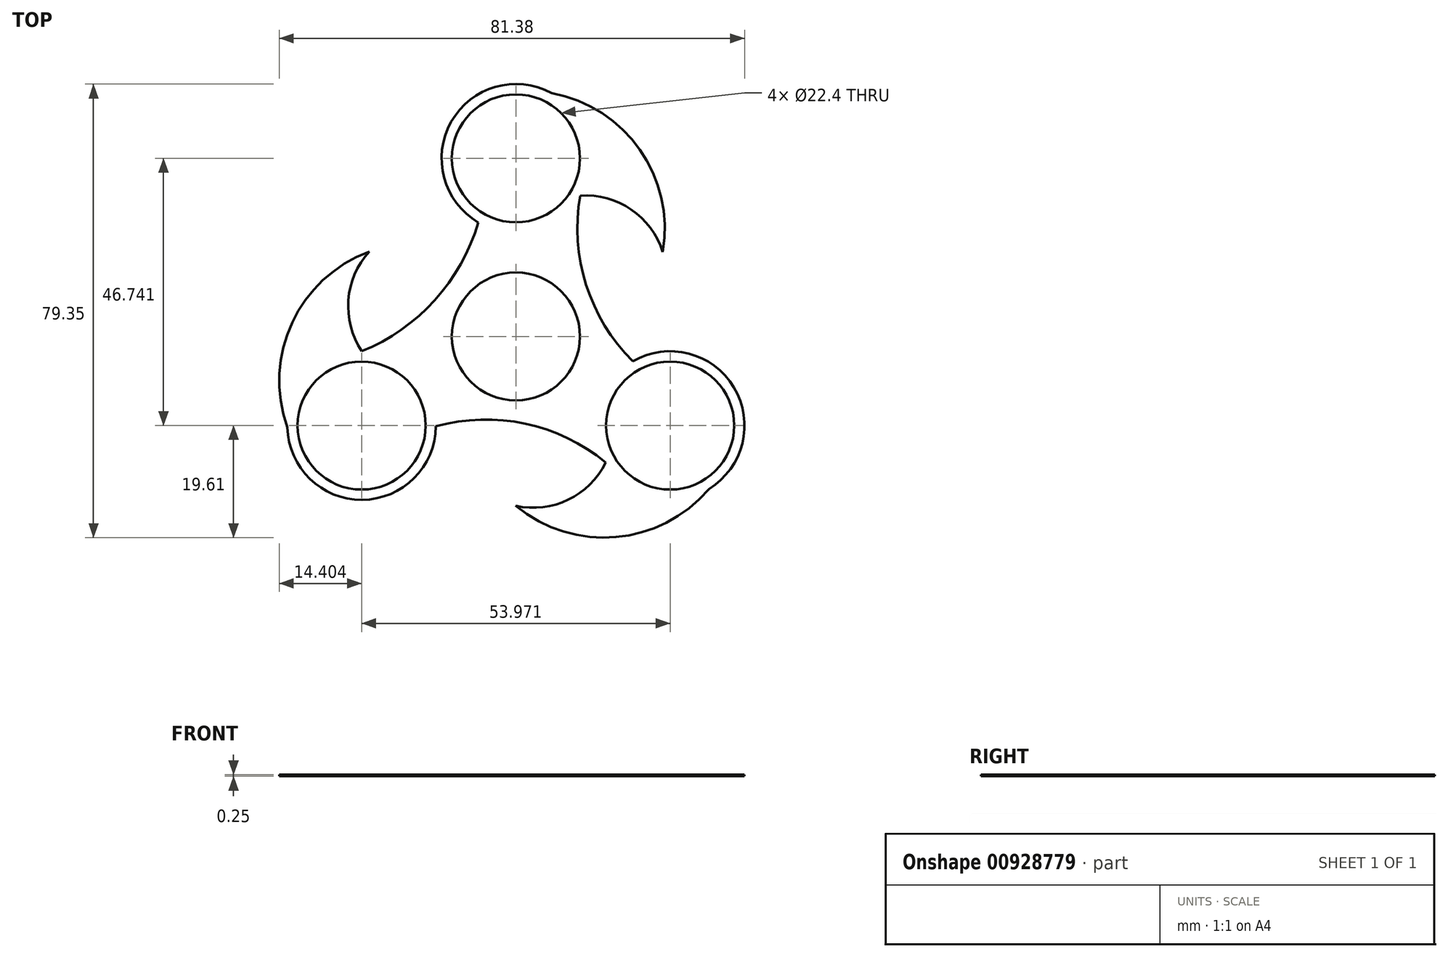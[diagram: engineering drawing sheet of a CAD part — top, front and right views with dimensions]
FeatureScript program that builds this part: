
annotation { "Feature Type Name" : "Feature", "Feature Type Description" : "" }
export const myFeature = defineFeature(function(context is Context, id is Id, definition is map)
    precondition{}
    {
        {
            var Q0;
            Q0=qCreatedBy(makeId("Top.planeOp"),FACE);
            var sketch = newSketch(context, id + "F0", { "sketchPlane" : qUnion([Q0])});
            skCircle(sketch, "E0", {"center": v(0, 0) * mm, "radius": 11.2 * mm});
            skCircle(sketch, "E1", {"center": v(0, 31.16) * mm, "radius": 11.2 * mm});
            skCircle(sketch, "E2", {"center": v(0, 31.16) * mm, "radius": 13 * mm});
            skCircle(sketch, "E3.1.0", {"center": v(-26.99, -15.58) * mm, "radius": 13 * mm});
            skCircle(sketch, "E4.1.0", {"center": v(-26.99, -15.58) * mm, "radius": 11.2 * mm});
            skCircle(sketch, "E4.2.0", {"center": v(26.99, -15.58) * mm, "radius": 11.2 * mm});
            skCircle(sketch, "E4.2.1", {"center": v(26.99, -15.58) * mm, "radius": 13 * mm});
            skArc(sketch, "E5", {"start": v(25.69, 14.79) * mm, "mid": v(21.66, 32.7) * mm, "end": v(6.2, 42.58) * mm});
            skArc(sketch, "E6", {"start": v(25.69, 14.79) * mm, "mid": v(20.16, 22.2) * mm, "end": v(11.24, 24.63) * mm});
            skArc(sketch, "E7.1.0", {"start": v(-25.64, 14.85) * mm, "mid": v(-29.3, 6.36) * mm, "end": v(-26.94, -2.58) * mm});
            skArc(sketch, "E7.1.1", {"start": v(-25.64, 14.85) * mm, "mid": v(-39.13, 2.41) * mm, "end": v(-39.97, -15.92) * mm});
            skArc(sketch, "E7.2.0", {"start": v(-0.03, -29.63) * mm, "mid": v(9.15, -28.56) * mm, "end": v(15.72, -22.04) * mm});
            skArc(sketch, "E7.2.1", {"start": v(-0.03, -29.63) * mm, "mid": v(17.49, -35.1) * mm, "end": v(33.78, -26.66) * mm});
            skArc(sketch, "E8", {"start": v(-26.94, -2.58) * mm, "mid": v(-14.2, 6.36) * mm, "end": v(-6.57, 19.94) * mm});
            skArc(sketch, "E9.1.0", {"start": v(15.72, -22.04) * mm, "mid": v(1.64, -15.26) * mm, "end": v(-13.99, -15.73) * mm});
            skArc(sketch, "E9.2.0", {"start": v(11.24, 24.63) * mm, "mid": v(12.38, 8.77) * mm, "end": v(20.8, -4.72) * mm});
            skSolve(sketch);
        }
        {
            var Q0;
            Q0=qSketchRegion(id+"F0",true);
            extrude(context, id + "F1", {"entities" : qUnion([Q0]), "depth" : .25 * mm, "offsetDistance" : 25 * mm});
        }
    });
